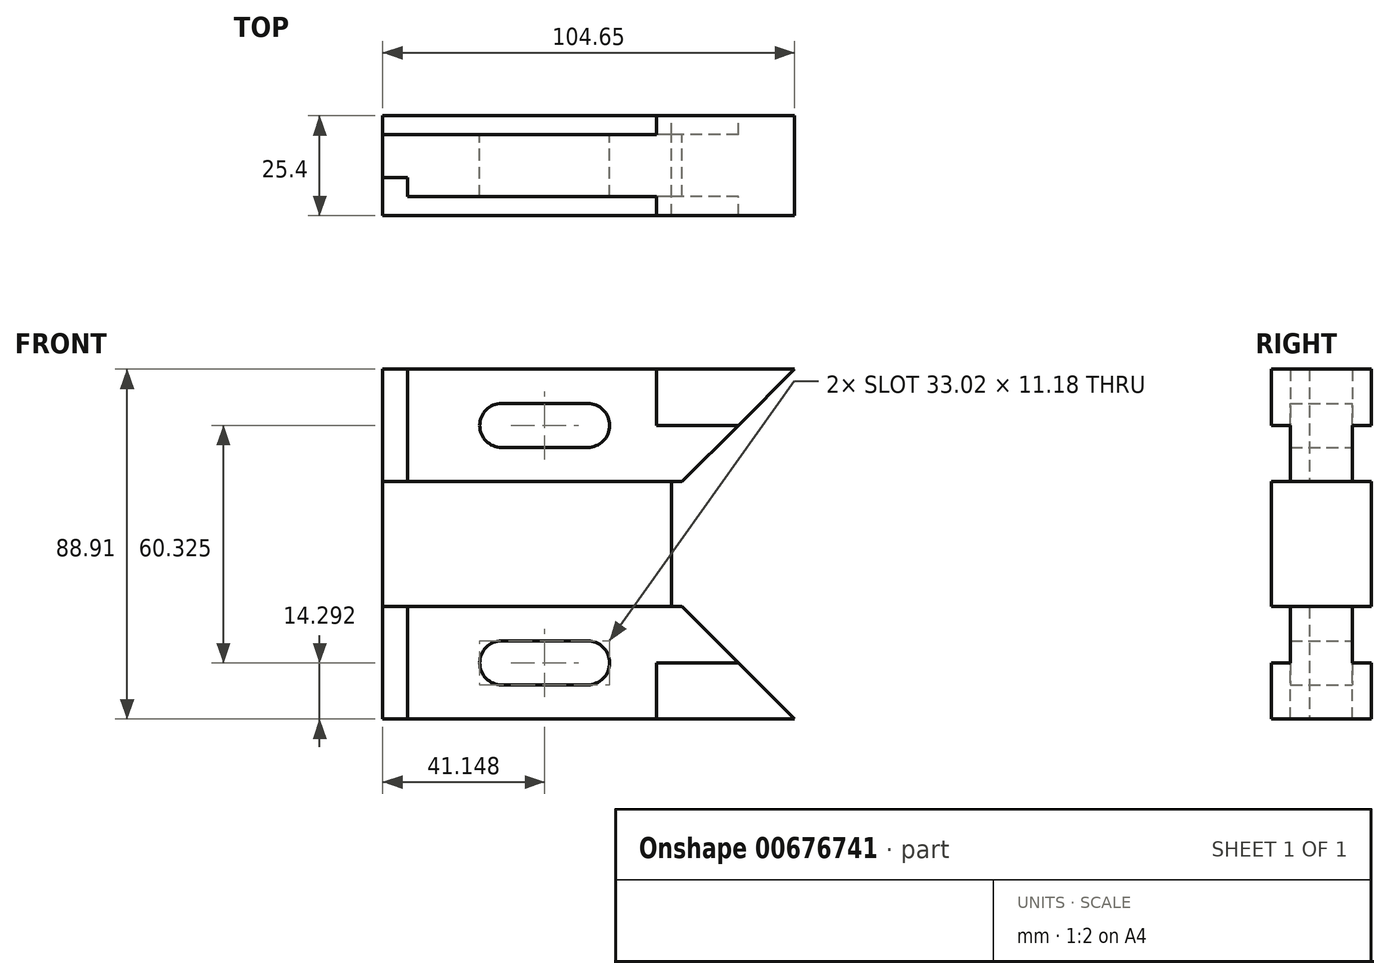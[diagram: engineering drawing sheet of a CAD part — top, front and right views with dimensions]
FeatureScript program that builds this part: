
annotation { "Feature Type Name" : "Feature", "Feature Type Description" : "" }
export const myFeature = defineFeature(function(context is Context, id is Id, definition is map)
    precondition{}
    {
        {
            var Q0;
            Q0=qCreatedBy(makeId("Front.planeOp"),FACE);
            var sketch = newSketch(context, id + "F0", { "sketchPlane" : qUnion([Q0])});
            skLineSegment(sketch, "E0.bottom", {"start": v(76.07, 0) * mm, "end": v(0, 0) * mm});
            skLineSegment(sketch, "E0.top", {"start": v(104.65, 28.58) * mm, "end": v(0, 28.57) * mm});
            skLineSegment(sketch, "E0.right", {"start": v(0, 0) * mm, "end": v(0, 28.57) * mm});
            skLineSegment(sketch, "E1.bottom", {"start": v(0, 0) * mm, "end": v(73.4, 0) * mm});
            skLineSegment(sketch, "E1.top", {"start": v(0, -15.87) * mm, "end": v(73.4, -15.87) * mm});
            skLineSegment(sketch, "E1.left", {"start": v(0, 0) * mm, "end": v(0, -15.87) * mm});
            skLineSegment(sketch, "E1.right", {"start": v(73.4, 0) * mm, "end": v(73.4, -15.87) * mm});
            skLineSegment(sketch, "E2", {"start": v(69.6, 28.57) * mm, "end": v(69.6, 14.29) * mm});
            skLineSegment(sketch, "E3", {"start": v(90.36, 14.29) * mm, "end": v(69.6, 14.29) * mm});
            skPoint(sketch, "E3.startSnap0", {"position": v(0, 14.29) * mm});
            skLineSegment(sketch, "E4", {"start": v(104.65, 28.58) * mm, "end": v(76.07, 0) * mm});
            skPoint(sketch, "E5.orphan", {"position": v(52.32, 14.29) * mm});
            skPoint(sketch, "E6.orphan", {"position": v(0, 0) * mm});
            skLineSegment(sketch, "E7", {"start": v(6.35, 28.57) * mm, "end": v(6.35, 0) * mm});
            skLineSegment(sketch, "E8.bottom", {"start": v(52.07, 8.7) * mm, "end": v(30.23, 8.7) * mm});
            skLineSegment(sketch, "E8.top", {"start": v(52.07, 19.88) * mm, "end": v(30.23, 19.88) * mm});
            skPoint(sketch, "E8.middle", {"position": v(41.15, 14.29) * mm});
            skArc(sketch, "E9", {"start": v(52.07, 8.7) * mm, "mid": v(57.66, 14.29) * mm, "end": v(52.07, 19.88) * mm});
            skArc(sketch, "E10", {"start": v(30.23, 19.88) * mm, "mid": v(24.64, 14.29) * mm, "end": v(30.23, 8.7) * mm});
            skSolve(sketch);
        }
        {
            var Q0;
            {var subQ3=sQuery(id+"F0.wireOp",EDGE,"E2");Q0=makeQuery(id+"F0.imprint","IMPRINT",FACE,{"disambiguationData":[TD([[makeQuery(id+"F0.imprint","IMPRINT",EDGE,{"derivedFrom":subQ3}),1.0]])]});}
            extrude(context, id + "F1", {"entities" : qUnion([Q0]), "endBound" : BoundingType.SYMMETRIC, "depth" : 25.4 * mm, "offsetDistance" : 25.4 * mm});
        }
        {
            var Q0;
            {var subQ2=sQuery(id+"F0.wireOp",EDGE,"E0.bottom");Q0=makeQuery(id+"F0.imprint","IMPRINT",FACE,{"disambiguationData":[TD([[makeQuery(id+"F0.imprint","IMPRINT",EDGE,{"derivedFrom":subQ2}),-1.0]])]});}
            extrude(context, id + "F2", {"entities" : qUnion([Q0]), "operationType" : NewBodyOperationType.ADD, "endBound" : BoundingType.SYMMETRIC, "depth" : 15.75 * mm, "offsetDistance" : 25.4 * mm});
        }
        {
            var Q0;
            {var subQ0=sQuery(id+"F0.wireOp",EDGE,"E0.right");Q0=makeQuery(id+"F0.imprint","IMPRINT",FACE,{"disambiguationData":[TD([[makeQuery(id+"F0.imprint","IMPRINT",EDGE,{"derivedFrom":subQ0}),-1.0]])]});}
            extrude(context, id + "F3", {"entities" : qUnion([Q0]), "operationType" : NewBodyOperationType.ADD, "depth" : 3.05 * mm, "offsetDistance" : 25.4 * mm, "hasSecondDirection" : true, "secondDirectionOppositeDirection" : true, "secondDirectionDepth" : 7.87 * mm});
        }
        {
            var Q0;
            Q0=makeQuery(id+"F0.imprint","IMPRINT",FACE,{"disambiguationData":[TD([[makeQuery(id+"F0.imprint","IMPRINT",EDGE,{"derivedFrom":sQuery(id+"F0.wireOp",EDGE,"E1.top")}),1.0]])]});
            extrude(context, id + "F4", {"entities" : qUnion([Q0]), "operationType" : NewBodyOperationType.ADD, "endBound" : BoundingType.SYMMETRIC, "depth" : 25.4 * mm, "offsetDistance" : 25.4 * mm});
        }
        {
            var Q0;
            Q0=makeQuery(id+"F1.opExtrude","SWEPT_BODY",BODY,{"disambiguationData":[OSD([sQuery(id+"F0.wireOp",EDGE,"E0.top"),sQuery(id+"F0.wireOp",EDGE,"E2"),sQuery(id+"F0.wireOp",EDGE,"E3"),sQuery(id+"F0.wireOp",EDGE,"E4")])]});
            var Q1;
            Q1=makeQuery(id+"F4.opExtrude","SWEPT_FACE",FACE,{"disambiguationData":[OSD([sQuery(id+"F0.wireOp",EDGE,"E1.top")])]});
            mirror(context, id + "F5", {"operationType" : NewBodyOperationType.ADD, "entities" : qUnion([Q0]), "mirrorPlane" : qUnion([Q1])});
        }
    });
